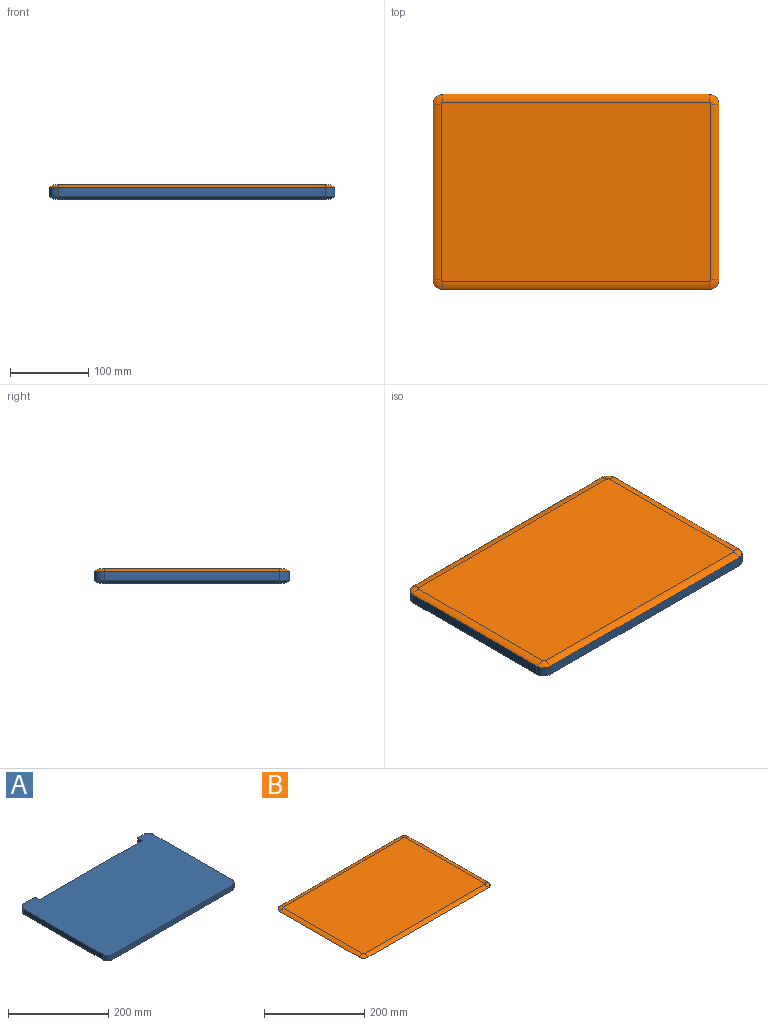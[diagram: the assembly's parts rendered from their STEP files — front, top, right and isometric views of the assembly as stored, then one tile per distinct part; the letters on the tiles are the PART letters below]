
ASSEMBLY  parts=2 mates=1
PART A: 23 faces, bbox 365.1x249.2x15.9 mm
  f0: plane 15.88x12.7mm, normal (-1,0,0), area 190.9mm2, adj f1,f3,f12,f13,f22
  f1: plane 289.94x15.88mm, normal (0,1,0), area 4602.9mm2, adj f0,f2,f3,f22
  f2: plane 15.88x12.7mm, normal (1,0,0), area 190.9mm2, adj f1,f3,f4,f14,f22
  f3: plane 344.06x228.18mm, normal (0,0,-1), area 77874.4mm2, adj f0,f1,f2,f4,f5,f6,f7,f8
  f4: cylinder r=19.05mm len=31.75mm, axis (-1,0,0), area 354.2mm2, adj f2,f3,f5,f14
  f5: torus R=2.17mm, axis (0,0,-1), area 133mm2, adj f3,f4,f6,f15
  f6: cylinder r=19.05mm len=223.84mm, axis (0,-1,0), area 2497.4mm2, adj f3,f5,f7,f16
  f7: torus R=2.17mm, axis (0,0,-1), area 133mm2, adj f3,f6,f8,f17
  f8: cylinder r=19.05mm len=339.73mm, axis (-1,0,0), area 3790.4mm2, adj f3,f7,f9,f18
  f9: torus R=2.17mm, axis (0,0,-1), area 133mm2, adj f3,f8,f10,f19
  f10: cylinder r=19.05mm len=223.84mm, axis (0,-1,0), area 2497.4mm2, adj f3,f9,f11,f20
  f11: torus R=2.17mm, axis (0,0,-1), area 133mm2, adj f3,f10,f12,f21
  f12: cylinder r=19.05mm len=18.03mm, axis (-1,0,0), area 201.2mm2, adj f0,f3,f11,f13
  f13: plane 18.03x12.7mm, normal (0,1,0), area 229mm2, adj f0,f12,f21,f22
  f14: plane 31.75x12.7mm, normal (0,1,0), area 403.2mm2, adj f2,f4,f15,f22
  f15: cylinder r=12.7mm len=12.7mm, axis (0,0,-1), area 253.4mm2, adj f5,f14,f16,f22
  f16: plane 223.84x12.7mm, normal (-1,0,0), area 2842.7mm2, adj f6,f15,f17,f22
  f17: cylinder r=12.7mm len=12.7mm, axis (0,0,-1), area 253.4mm2, adj f7,f16,f18,f22
  f18: plane 339.73x12.7mm, normal (0,-1,0), area 4314.5mm2, adj f8,f17,f19,f22
  f19: cylinder r=12.7mm len=12.7mm, axis (0,0,-1), area 253.4mm2, adj f9,f18,f20,f22
  f20: plane 223.84x12.7mm, normal (1,0,0), area 2842.7mm2, adj f10,f19,f21,f22
  f21: cylinder r=12.7mm len=12.7mm, axis (0,0,-1), area 253.4mm2, adj f11,f13,f20,f22
  f22: plane 365.13x249.24mm, normal (0,0,1), area 87182.1mm2, adj f0,f1,f2,f13,f14,f15,f16,f17
PART B: 15 faces, bbox 365.1x249.2x18.3 mm
  f0: plane 365.13x249.24mm, normal (0,0,-1), area 87182.1mm2, adj f2,f3,f4,f5,f6,f7,f8,f9
  f1: plane 344.06x228.18mm, normal (0,0,1), area 78503.5mm2, adj f2,f3,f4,f5,f6,f7,f8,f9
  f2: cylinder r=19.05mm len=339.73mm, axis (-1,0,0), area 3790.4mm2, adj f0,f1,f3,f4,f14
  f3: torus R=2.17mm, axis (0,0,-1), area 133mm2, adj f0,f1,f2,f5
  f4: torus R=2.17mm, axis (0,0,-1), area 133mm2, adj f0,f1,f2,f6
  f5: cylinder r=19.05mm len=223.84mm, axis (0,-1,0), area 2497.4mm2, adj f0,f1,f3,f7
  f6: cylinder r=19.05mm len=223.84mm, axis (0,-1,0), area 2497.4mm2, adj f0,f1,f4,f8
  f7: torus R=2.17mm, axis (0,0,-1), area 133mm2, adj f0,f1,f5,f9
  f8: torus R=2.17mm, axis (0,0,-1), area 133mm2, adj f0,f1,f6,f9
  f9: cylinder r=19.05mm len=339.73mm, axis (-1,0,0), area 3790.4mm2, adj f0,f1,f7,f8
  f10: plane 15.17x12.7mm, normal (-1,0,0), area 175.3mm2, adj f0,f11,f13,f14
  f11: plane 289.94x8.82mm, normal (0,-1,0), area 2556.5mm2, adj f0,f10,f12,f13
  f12: plane 15.17x12.7mm, normal (1,0,0), area 175.3mm2, adj f0,f11,f13,f14
  f13: cylinder r=6.35mm len=289.94mm, axis (1,0,0), area 5784.1mm2, adj f10,f11,f12,f14
  f14: plane 289.94x8.82mm, normal (0,1,0), area 2556.5mm2, adj f2,f10,f12,f13
PLACE A at identity fixed
PLACE B rot(axis=(-1,0,0),0deg) t=(0,0,0)mm
MATE revolute A.f0 <-> B.f13  axis (1,0,0) through (151.83,118.27,7.06)mm
